# Revit family: Conjunto de pilotaje valvulas direccionales eléctricas_Aguilera Electronica
name_source: partatom
category: Equipos eléctricos
revit_build: Autodesk Revit 2017 (Build: 20160225_1515(x64)
units: mm (PartAtom-declared; Revit-internal decimal feet)

## family parameters
Anfitrión = Cara
Compartido = No
Corte con vacíos al cargar = No
Cota de conector redondo = Diámetro de uso
Número OmniClass = 23.65.55.00
Punto de cálculo de habitación = No
Tipo de pieza = Interruptor de equipos
Título OmniClass = Distribution of Supplied Liquids/Gases

## types (1)
- Conjunto de pilotaje para 1 válvula direccional eléctrica
    Alto = 200 mm  [stored 0.656168 ft]
    Ancho = 150 mm
    Descripción = Conjunto de pilotaje independiente que debe llevar cada válvula direccional, mecanizado en caja plástica.
Características:

    Entrada de control de extinción del panel de extinción.
    Entrada control de selección de riesgo del cuadro de bombas de agua nebulizada y señal de alimentación 230 Vca.
    Salida vigilada de activación (230 Vca) de la electroválvula direccional (control permanete de su conexión).
    Entrada vigilada de pulsador de disparo remoto.
    Entrada vigilada de pulsador de bloqueo remoto.
    Entrada vigilada de control de estado de la válvula bypass.
    Diámetro tubo = 20 mm  [stored 0.0656168 ft]
    Elevación por defecto = 1200 mm
    Fabricante = Aguilera Extinción
    Fondo = 123 mm  [stored 0.403543 ft]
    Modelo = AN/CVDPE
    Potencia aparente = 230 VA
    Potencial eléctrico = 230 V
    Símbolo = Sí
    Símbolo texto modelo = Sí
    URL = http://aguilera.es

note: [stored X ft] marks values corroborated as IEEE doubles in the binary element streams (Revit-internal decimal feet)
